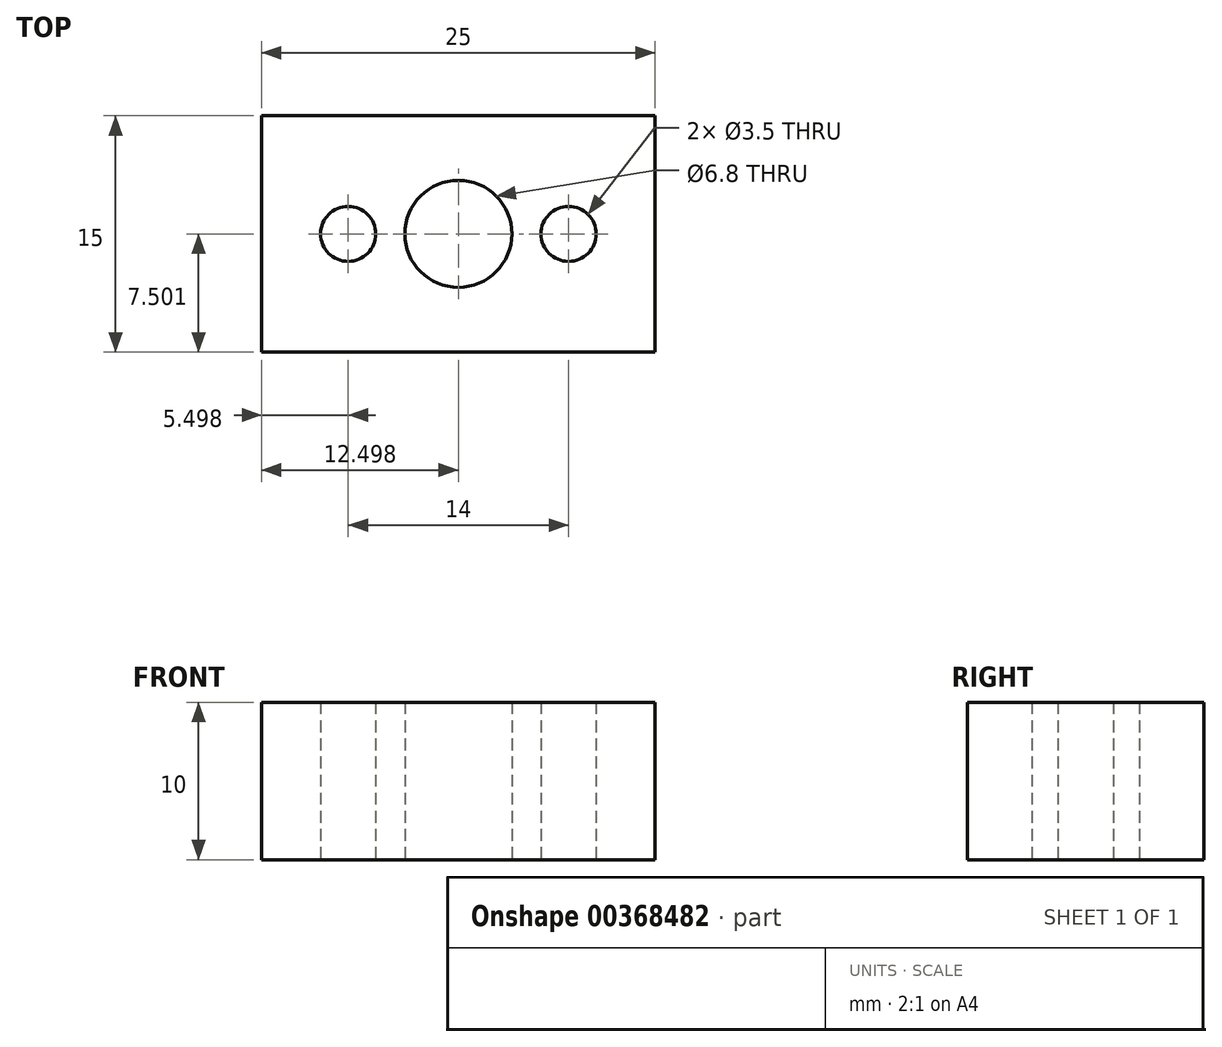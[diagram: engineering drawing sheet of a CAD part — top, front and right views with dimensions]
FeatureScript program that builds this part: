
annotation { "Feature Type Name" : "Feature", "Feature Type Description" : "" }
export const myFeature = defineFeature(function(context is Context, id is Id, definition is map)
    precondition{}
    {
        {
            var Q0;
            Q0=qCreatedBy(makeId("Top.planeOp"),FACE);
            var sketch = newSketch(context, id + "F0", { "sketchPlane" : qUnion([Q0])});
            skLineSegment(sketch, "E0.bottom", {"start": v(-13.73, 11.73) * mm, "end": v(11.27, 11.73) * mm});
            skLineSegment(sketch, "E0.top", {"start": v(-13.73, -3.27) * mm, "end": v(11.27, -3.27) * mm});
            skLineSegment(sketch, "E0.left", {"start": v(-13.73, 11.73) * mm, "end": v(-13.73, -3.27) * mm});
            skLineSegment(sketch, "E0.right", {"start": v(11.27, 11.73) * mm, "end": v(11.27, -3.27) * mm});
            skCircle(sketch, "E1", {"center": v(-1.23, 4.23) * mm, "radius": 3.4 * mm});
            skCircle(sketch, "E2", {"center": v(5.77, 4.23) * mm, "radius": 1.75 * mm});
            skCircle(sketch, "E3", {"center": v(-8.23, 4.23) * mm, "radius": 1.75 * mm});
            skSolve(sketch);
        }
        {
            var Q0;
            Q0 = qSketchRegion(id + "F0", true);
            extrude(context, id + "F1", {"entities" : qUnion([Q0]), "depth" : 10 * mm});
        }
    });
